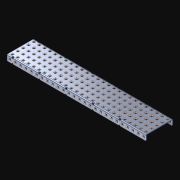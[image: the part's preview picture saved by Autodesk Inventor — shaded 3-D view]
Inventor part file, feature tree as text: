
AUTODESK INVENTOR PART (.ipt)
format: ipt  version: 2021 (Build 250183000, 183)  size: 2,202,112 bytes
history: native  units: in
note: dims shown in document units (in); Inventor stores cm internally (conversion verified against a paired STEP export)
features: extrude x183, other x183, sketch x4, pattern_linear x3
ambient origin geometry x8: Origin, YZ Plane, XZ Plane, XY Plane, X Axis, Y Axis, Z Axis, Center Point
bodies: Solid1 (feature_tree)
feature tree (373):
  pattern_linear  "Rectangular Pattern1"  Spacing1=0.182in  [1 undecoded]
  pattern_linear  "Rectangular Pattern2"  Spacing1=0.046in  [1 undecoded]
  pattern_linear  "Rectangular Pattern3"  Spacing1=0.5in  [1 undecoded]
  extrude  "Extrusion1"  Depth=0.046in
  sketch  "Sketch1"  dims[d0=0.182in]
  other  "Srf1"
  sketch  "Sketch2"  dims[d1=0.046in d2=0.0in]
  other  "Srf2"
  sketch  "Sketch3"  dims[d3=0.182in]
  other  "Srf3"
  other  "Srf4"
  other  "Srf5"
  other  "Srf6"
  other  "Srf7"
  other  "Srf8"
  other  "Srf9"
  other  "Srf10"
  other  "Srf11"
  other  "Srf12"
  other  "Srf13"
  other  "Srf14"
  other  "Srf15"
  other  "Srf16"
  other  "Srf17"
  other  "Srf18"
  other  "Srf19"
  other  "Srf20"
  other  "Srf21"
  other  "Srf22"
  other  "Srf23"
  other  "Srf24"
  other  "Srf25"
  other  "Srf26"
  other  "Srf27"
  other  "Srf28"
  other  "Srf38"
  other  "Srf39"
  other  "Srf40"
  other  "Srf41"
  other  "Srf42"
  other  "Srf43"
  other  "Srf44"
  other  "Srf45"
  other  "Srf46"
  other  "Srf47"
  other  "Srf48"
  other  "Srf49"
  other  "Srf50"
  other  "Srf51"
  other  "Srf52"
  other  "Srf53"
  other  "Srf54"
  other  "Srf55"
  other  "Srf56"
  other  "Srf57"
  other  "Srf58"
  other  "Srf59"
  other  "Srf60"
  other  "Srf61"
  other  "Srf62"
  other  "Srf72"
  other  "Srf73"
  other  "Srf74"
  other  "Srf75"
  other  "Srf76"
  other  "Srf77"
  other  "Srf78"
  other  "Srf79"
  other  "Srf80"
  other  "Srf81"
  other  "Srf82"
  other  "Srf83"
  other  "Srf84"
  other  "Srf85"
  other  "Srf86"
  other  "Srf87"
  other  "Srf88"
  other  "Srf89"
  other  "Srf90"
  other  "Srf91"
  other  "Srf92"
  other  "Srf93"
  other  "Srf94"
  other  "Srf95"
  other  "Srf96"
  other  "Srf97"
  other  "Srf107"
  other  "Srf108"
  other  "Srf109"
  other  "Srf110"
  other  "Srf111"
  other  "Srf112"
  other  "Srf113"
  other  "Srf114"
  other  "Srf115"
  other  "Srf116"
  other  "Srf117"
  other  "Srf118"
  other  "Srf119"
  other  "Srf120"
  other  "Srf121"
  other  "Srf122"
  other  "Srf123"
  other  "Srf124"
  other  "Srf125"
  other  "Srf126"
  other  "Srf127"
  other  "Srf128"
  other  "Srf129"
  other  "Srf130"
  other  "Srf131"
  other  "Srf132"
  other  "Srf142"
  other  "Srf143"
  other  "Srf144"
  other  "Srf145"
  other  "Srf146"
  other  "Srf147"
  other  "Srf148"
  other  "Srf149"
  other  "Srf150"
  other  "Srf151"
  other  "Srf152"
  other  "Srf153"
  other  "Srf154"
  other  "Srf155"
  other  "Srf156"
  other  "Srf157"
  other  "Srf158"
  other  "Srf159"
  other  "Srf160"
  other  "Srf161"
  other  "Srf162"
  other  "Srf163"
  other  "Srf164"
  other  "Srf165"
  other  "Srf166"
  other  "Srf167"
  other  "Srf177"
  other  "Srf178"
  other  "Srf179"
  other  "Srf180"
  other  "Srf181"
  other  "Srf182"
  other  "Srf183"
  other  "Srf184"
  other  "Srf185"
  other  "Srf186"
  other  "Srf187"
  other  "Srf188"
  other  "Srf189"
  other  "Srf190"
  other  "Srf191"
  other  "Srf192"
  other  "Srf193"
  other  "Srf194"
  other  "Srf195"
  other  "Srf196"
  other  "Srf197"
  other  "Srf198"
  other  "Srf199"
  other  "Srf200"
  other  "Srf201"
  other  "Srf202"
  other  "Srf212"
  other  "Srf213"
  other  "Srf214"
  other  "Srf215"
  other  "Srf216"
  other  "Srf217"
  other  "Srf218"
  other  "Srf219"
  other  "Srf220"
  other  "Srf221"
  other  "Srf222"
  other  "Srf223"
  other  "Srf224"
  other  "Srf225"
  other  "Srf226"
  other  "Srf227"
  other  "Srf228"
  other  "Srf229"
  other  "Srf230"
  other  "Srf231"
  other  "Srf232"
  other  "Srf233"
  other  "Srf234"
  other  "Srf235"
  other  "Srf236"
  sketch  "Sketch4"  dims[d4=0.046in d5=0.0in d6=0.182in d7=0.046in d8=0.0in d11=0.5in d12=10.2362in d14=0.5in d15=1.9685in d17=0.5in d18=10.2362in d20=0.5in d21=4.5in d22=0.0in]
  parser-record x1  (decoder bookkeeping rows leaked as tree rows — omitted from the tree; the rows remain in map.json)
  extrude  "ExtrusionSrf1"  Depth=0.046in
  extrude  "ExtrusionSrf2"  Depth=0.046in
  extrude  "ExtrusionSrf3"  Depth=0.046in
  extrude  "ExtrusionSrf4"  Depth=0.046in
  extrude  "ExtrusionSrf5"  Depth=0.046in
  extrude  "ExtrusionSrf6"  TaperAngle=0.0deg  [1 undecoded]
  extrude  "ExtrusionSrf7"  [1 undecoded]
  extrude  "ExtrusionSrf8"  [1 undecoded]
  extrude  "ExtrusionSrf9"  [1 undecoded]
  extrude  "ExtrusionSrf10"  [1 undecoded]
  extrude  "ExtrusionSrf11"  [1 undecoded]
  extrude  "ExtrusionSrf12"  [1 undecoded]
  extrude  "ExtrusionSrf13"  [1 undecoded]
  extrude  "ExtrusionSrf14"  [1 undecoded]
  extrude  "ExtrusionSrf15"  [1 undecoded]
  extrude  "ExtrusionSrf16"  [1 undecoded]
  extrude  "ExtrusionSrf17"  [1 undecoded]
  extrude  "ExtrusionSrf18"  [1 undecoded]
  extrude  "ExtrusionSrf19"  [1 undecoded]
  extrude  "ExtrusionSrf20"  [1 undecoded]
  extrude  "ExtrusionSrf21"  [1 undecoded]
  extrude  "ExtrusionSrf22"  [1 undecoded]
  extrude  "ExtrusionSrf23"  [1 undecoded]
  extrude  "ExtrusionSrf24"  [1 undecoded]
  extrude  "ExtrusionSrf25"  [1 undecoded]
  extrude  "ExtrusionSrf26"  [1 undecoded]
  extrude  "ExtrusionSrf27"  [1 undecoded]
  extrude  "ExtrusionSrf28"  [1 undecoded]
  extrude  "ExtrusionSrf38"  [1 undecoded]
  extrude  "ExtrusionSrf39"  [1 undecoded]
  extrude  "ExtrusionSrf40"  [1 undecoded]
  extrude  "ExtrusionSrf41"  [1 undecoded]
  extrude  "ExtrusionSrf42"  [1 undecoded]
  extrude  "ExtrusionSrf43"  [1 undecoded]
  extrude  "ExtrusionSrf44"  [1 undecoded]
  extrude  "ExtrusionSrf45"  [1 undecoded]
  extrude  "ExtrusionSrf46"  [1 undecoded]
  extrude  "ExtrusionSrf47"  [1 undecoded]
  extrude  "ExtrusionSrf48"  [1 undecoded]
  extrude  "ExtrusionSrf49"  [1 undecoded]
  extrude  "ExtrusionSrf50"  [1 undecoded]
  extrude  "ExtrusionSrf51"  [1 undecoded]
  extrude  "ExtrusionSrf52"  [1 undecoded]
  extrude  "ExtrusionSrf53"  [1 undecoded]
  extrude  "ExtrusionSrf54"  [1 undecoded]
  extrude  "ExtrusionSrf55"  [1 undecoded]
  extrude  "ExtrusionSrf56"  [1 undecoded]
  extrude  "ExtrusionSrf57"  [1 undecoded]
  extrude  "ExtrusionSrf58"  [1 undecoded]
  extrude  "ExtrusionSrf59"  [1 undecoded]
  extrude  "ExtrusionSrf60"  [1 undecoded]
  extrude  "ExtrusionSrf61"  [1 undecoded]
  extrude  "ExtrusionSrf62"  [1 undecoded]
  extrude  "ExtrusionSrf72"  [1 undecoded]
  extrude  "ExtrusionSrf73"  [1 undecoded]
  extrude  "ExtrusionSrf74"  [1 undecoded]
  extrude  "ExtrusionSrf75"  [1 undecoded]
  extrude  "ExtrusionSrf76"  [1 undecoded]
  extrude  "ExtrusionSrf77"  [1 undecoded]
  extrude  "ExtrusionSrf78"  [1 undecoded]
  extrude  "ExtrusionSrf79"  [1 undecoded]
  extrude  "ExtrusionSrf80"  [1 undecoded]
  extrude  "ExtrusionSrf81"  [1 undecoded]
  extrude  "ExtrusionSrf82"  [1 undecoded]
  extrude  "ExtrusionSrf83"  [1 undecoded]
  extrude  "ExtrusionSrf84"  [1 undecoded]
  extrude  "ExtrusionSrf85"  [1 undecoded]
  extrude  "ExtrusionSrf86"  [1 undecoded]
  extrude  "ExtrusionSrf87"  [1 undecoded]
  extrude  "ExtrusionSrf88"  [1 undecoded]
  extrude  "ExtrusionSrf89"  [1 undecoded]
  extrude  "ExtrusionSrf90"  [1 undecoded]
  extrude  "ExtrusionSrf91"  [1 undecoded]
  extrude  "ExtrusionSrf92"  [1 undecoded]
  extrude  "ExtrusionSrf93"  [1 undecoded]
  extrude  "ExtrusionSrf94"  [1 undecoded]
  extrude  "ExtrusionSrf95"  [1 undecoded]
  extrude  "ExtrusionSrf96"  [1 undecoded]
  extrude  "ExtrusionSrf97"  [1 undecoded]
  extrude  "ExtrusionSrf107"  [1 undecoded]
  extrude  "ExtrusionSrf108"  [1 undecoded]
  extrude  "ExtrusionSrf109"  [1 undecoded]
  extrude  "ExtrusionSrf110"  [1 undecoded]
  extrude  "ExtrusionSrf111"  [1 undecoded]
  extrude  "ExtrusionSrf112"  [1 undecoded]
  extrude  "ExtrusionSrf113"  [1 undecoded]
  extrude  "ExtrusionSrf114"  [1 undecoded]
  extrude  "ExtrusionSrf115"  [1 undecoded]
  extrude  "ExtrusionSrf116"  [1 undecoded]
  extrude  "ExtrusionSrf117"  [1 undecoded]
  extrude  "ExtrusionSrf118"  [1 undecoded]
  extrude  "ExtrusionSrf119"  [1 undecoded]
  extrude  "ExtrusionSrf120"  [1 undecoded]
  extrude  "ExtrusionSrf121"  [1 undecoded]
  extrude  "ExtrusionSrf122"  [1 undecoded]
  extrude  "ExtrusionSrf123"  [1 undecoded]
  extrude  "ExtrusionSrf124"  [1 undecoded]
  extrude  "ExtrusionSrf125"  [1 undecoded]
  extrude  "ExtrusionSrf126"  [1 undecoded]
  extrude  "ExtrusionSrf127"  [1 undecoded]
  extrude  "ExtrusionSrf128"  [1 undecoded]
  extrude  "ExtrusionSrf129"  [1 undecoded]
  extrude  "ExtrusionSrf130"  [1 undecoded]
  extrude  "ExtrusionSrf131"  [1 undecoded]
  extrude  "ExtrusionSrf132"  [1 undecoded]
  extrude  "ExtrusionSrf142"  [1 undecoded]
  extrude  "ExtrusionSrf143"  [1 undecoded]
  extrude  "ExtrusionSrf144"  [1 undecoded]
  extrude  "ExtrusionSrf145"  [1 undecoded]
  extrude  "ExtrusionSrf146"  [1 undecoded]
  extrude  "ExtrusionSrf147"  [1 undecoded]
  extrude  "ExtrusionSrf148"  [1 undecoded]
  extrude  "ExtrusionSrf149"  [1 undecoded]
  extrude  "ExtrusionSrf150"  [1 undecoded]
  extrude  "ExtrusionSrf151"  [1 undecoded]
  extrude  "ExtrusionSrf152"  [1 undecoded]
  extrude  "ExtrusionSrf153"  [1 undecoded]
  extrude  "ExtrusionSrf154"  [1 undecoded]
  extrude  "ExtrusionSrf155"  [1 undecoded]
  extrude  "ExtrusionSrf156"  [1 undecoded]
  extrude  "ExtrusionSrf157"  [1 undecoded]
  extrude  "ExtrusionSrf158"  [1 undecoded]
  extrude  "ExtrusionSrf159"  [1 undecoded]
  extrude  "ExtrusionSrf160"  [1 undecoded]
  extrude  "ExtrusionSrf161"  [1 undecoded]
  extrude  "ExtrusionSrf162"  [1 undecoded]
  extrude  "ExtrusionSrf163"  [1 undecoded]
  extrude  "ExtrusionSrf164"  [1 undecoded]
  extrude  "ExtrusionSrf165"  [1 undecoded]
  extrude  "ExtrusionSrf166"  [1 undecoded]
  extrude  "ExtrusionSrf167"  [1 undecoded]
  extrude  "ExtrusionSrf177"  [1 undecoded]
  extrude  "ExtrusionSrf178"  [1 undecoded]
  extrude  "ExtrusionSrf179"  [1 undecoded]
  extrude  "ExtrusionSrf180"  [1 undecoded]
  extrude  "ExtrusionSrf181"  [1 undecoded]
  extrude  "ExtrusionSrf182"  [1 undecoded]
  extrude  "ExtrusionSrf183"  [1 undecoded]
  extrude  "ExtrusionSrf184"  [1 undecoded]
  extrude  "ExtrusionSrf185"  [1 undecoded]
  extrude  "ExtrusionSrf186"  [1 undecoded]
  extrude  "ExtrusionSrf187"  [1 undecoded]
  extrude  "ExtrusionSrf188"  [1 undecoded]
  extrude  "ExtrusionSrf189"  [1 undecoded]
  extrude  "ExtrusionSrf190"  [1 undecoded]
  extrude  "ExtrusionSrf191"  [1 undecoded]
  extrude  "ExtrusionSrf192"  [1 undecoded]
  extrude  "ExtrusionSrf193"  [1 undecoded]
  extrude  "ExtrusionSrf194"  [1 undecoded]
  extrude  "ExtrusionSrf195"  [1 undecoded]
  extrude  "ExtrusionSrf196"  [1 undecoded]
  extrude  "ExtrusionSrf197"  [1 undecoded]
  extrude  "ExtrusionSrf198"  [1 undecoded]
  extrude  "ExtrusionSrf199"  [1 undecoded]
  extrude  "ExtrusionSrf200"  [1 undecoded]
  extrude  "ExtrusionSrf201"  [1 undecoded]
  extrude  "ExtrusionSrf202"  [1 undecoded]
  extrude  "ExtrusionSrf212"  [1 undecoded]
  extrude  "ExtrusionSrf213"  [1 undecoded]
  extrude  "ExtrusionSrf214"  [1 undecoded]
  extrude  "ExtrusionSrf215"  [1 undecoded]
  extrude  "ExtrusionSrf216"  [1 undecoded]
  extrude  "ExtrusionSrf217"  [1 undecoded]
  extrude  "ExtrusionSrf218"  [1 undecoded]
  extrude  "ExtrusionSrf219"  [1 undecoded]
  extrude  "ExtrusionSrf220"  [1 undecoded]
  extrude  "ExtrusionSrf221"  [1 undecoded]
  extrude  "ExtrusionSrf222"  [1 undecoded]
  extrude  "ExtrusionSrf223"  [1 undecoded]
  extrude  "ExtrusionSrf224"  [1 undecoded]
  extrude  "ExtrusionSrf225"  [1 undecoded]
  extrude  "ExtrusionSrf226"  [1 undecoded]
  extrude  "ExtrusionSrf227"  [1 undecoded]
  extrude  "ExtrusionSrf228"  [1 undecoded]
  extrude  "ExtrusionSrf229"  [1 undecoded]
  extrude  "ExtrusionSrf230"  [1 undecoded]
  extrude  "ExtrusionSrf231"  [1 undecoded]
  extrude  "ExtrusionSrf232"  [1 undecoded]
  extrude  "ExtrusionSrf233"  [1 undecoded]
  extrude  "ExtrusionSrf234"  [1 undecoded]
  extrude  "ExtrusionSrf235"  [1 undecoded]
  extrude  "ExtrusionSrf236"  [1 undecoded]
note: 180 required parameter values undecoded (feature->parameter linkage not recoverable at this tier; creation-order binding heuristic only, values carry confidence <= 0.55)
